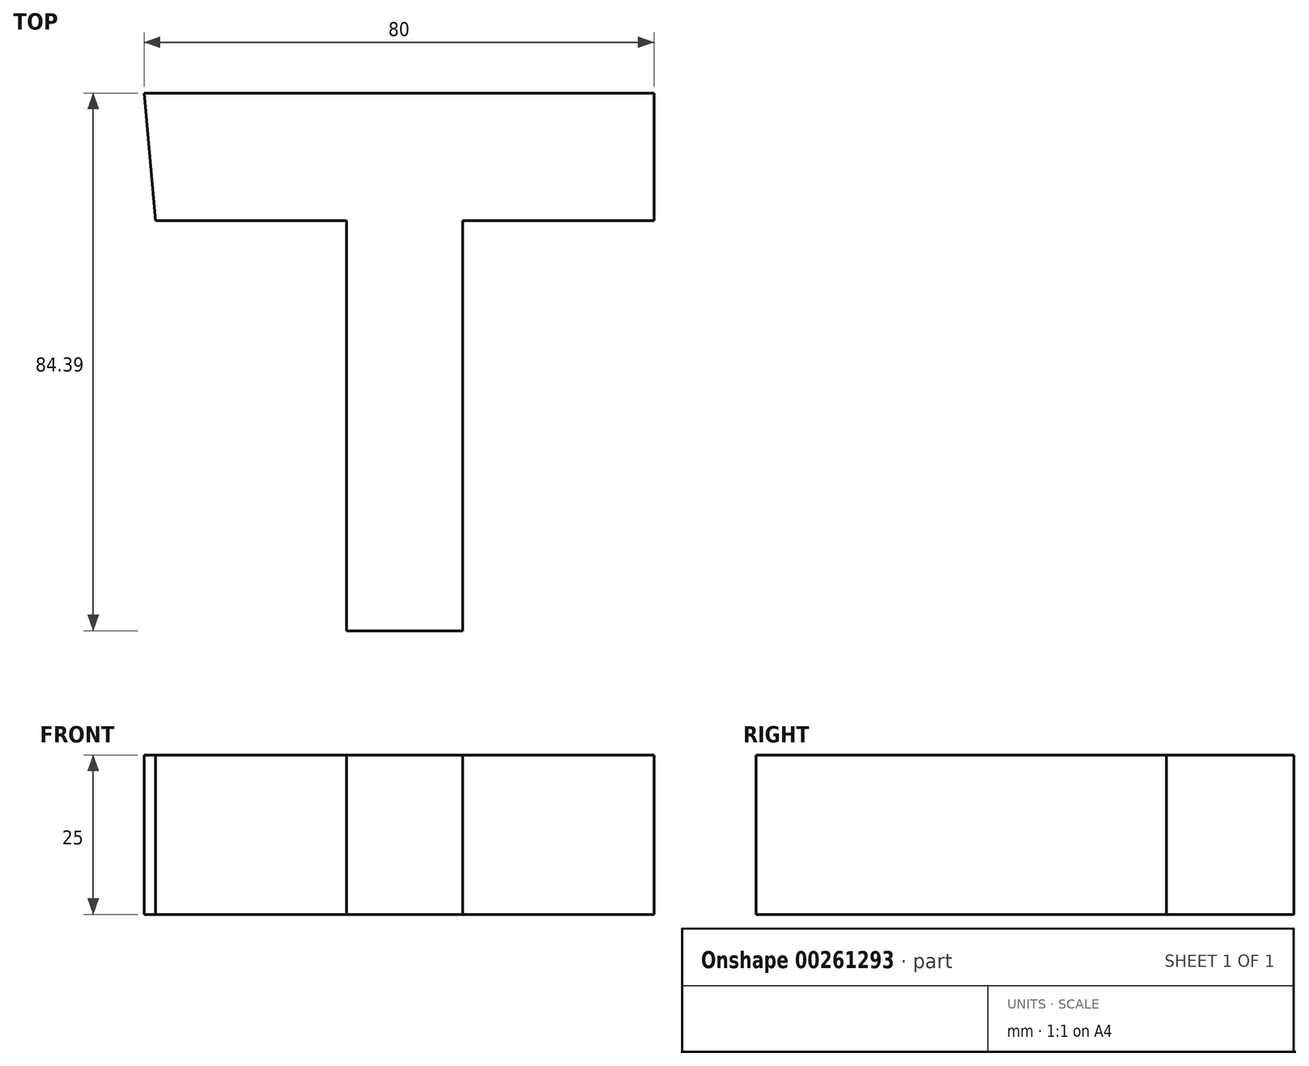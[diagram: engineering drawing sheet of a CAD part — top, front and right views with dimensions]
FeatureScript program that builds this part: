
annotation { "Feature Type Name" : "Feature", "Feature Type Description" : "" }
export const myFeature = defineFeature(function(context is Context, id is Id, definition is map)
    precondition{}
    {
        {
            var Q0;
            Q0=qCreatedBy(makeId("Top.planeOp"),FACE);
            var sketch = newSketch(context, id + "F0", { "sketchPlane" : qUnion([Q0])});
            skLineSegment(sketch, "E0", {"start": v(-48.45, 51.21) * mm, "end": v(31.55, 51.21) * mm});
            skLineSegment(sketch, "E1", {"start": v(31.55, 51.21) * mm, "end": v(31.55, 31.21) * mm});
            skLineSegment(sketch, "E2", {"start": v(31.55, 31.21) * mm, "end": v(1.55, 31.21) * mm});
            skLineSegment(sketch, "E3", {"start": v(1.55, 31.21) * mm, "end": v(1.55, -33.18) * mm});
            skLineSegment(sketch, "E4", {"start": v(1.55, -33.18) * mm, "end": v(-16.66, -33.18) * mm});
            skLineSegment(sketch, "E5", {"start": v(-16.66, -33.18) * mm, "end": v(-16.66, 31.21) * mm});
            skLineSegment(sketch, "E6", {"start": v(-16.66, 31.21) * mm, "end": v(-46.66, 31.21) * mm});
            skLineSegment(sketch, "E7", {"start": v(-46.66, 31.21) * mm, "end": v(-48.45, 51.21) * mm});
            skSolve(sketch);
        }
        {
            var Q0;
            Q0 = qSketchRegion(id + "F0", true);
            extrude(context, id + "F1", {"entities" : qUnion([Q0]), "depth" : 25 * mm});
        }
    });
